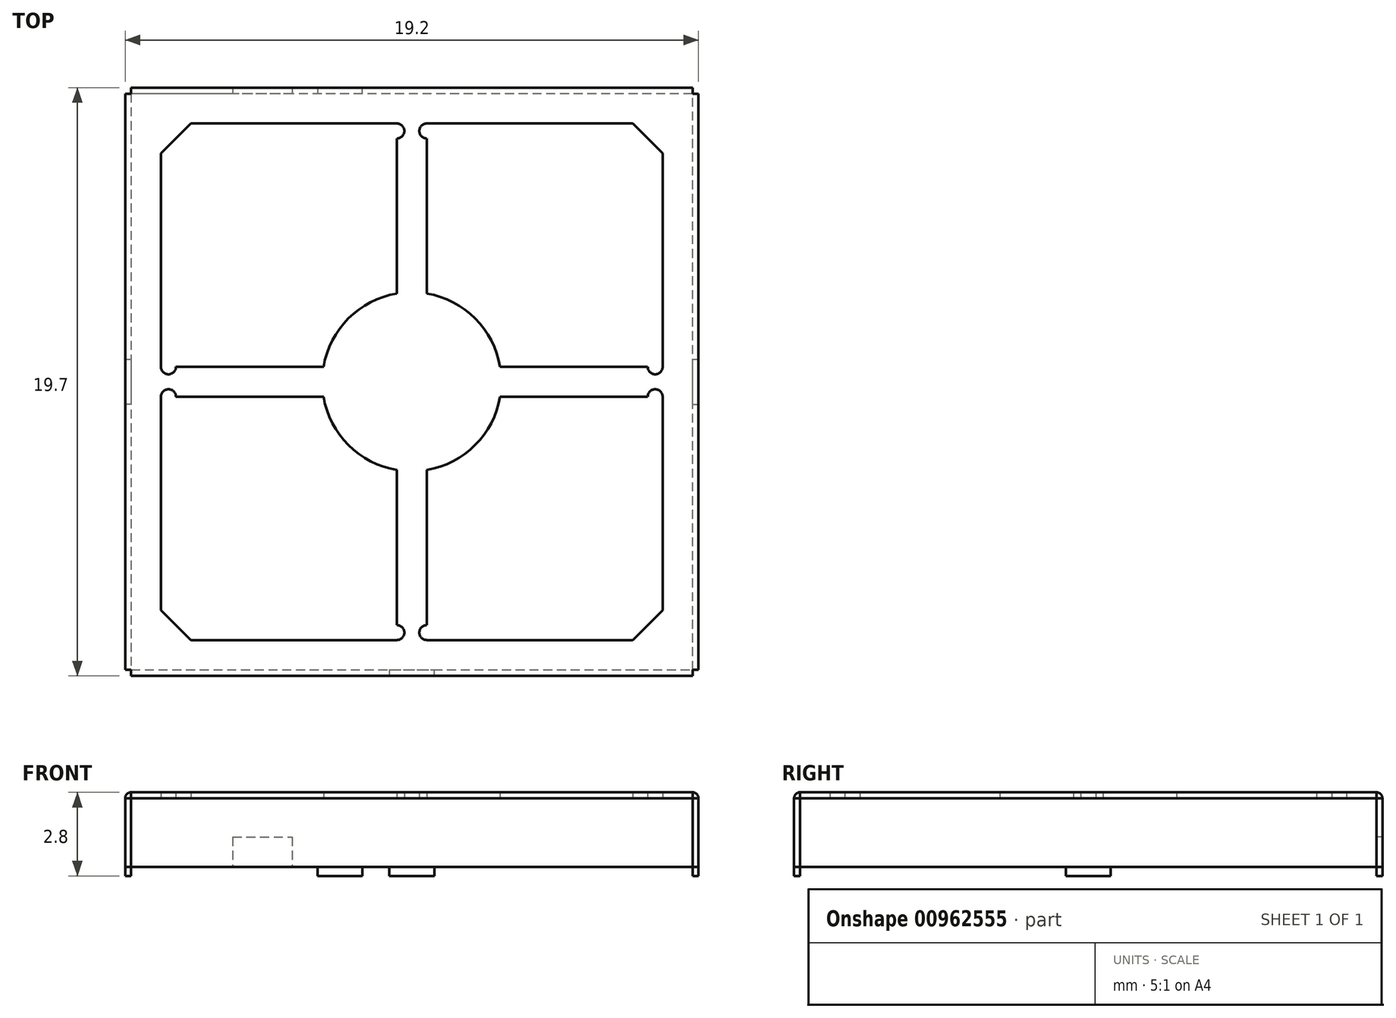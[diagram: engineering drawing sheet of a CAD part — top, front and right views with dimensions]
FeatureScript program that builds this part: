
annotation { "Feature Type Name" : "Feature", "Feature Type Description" : "" }
export const myFeature = defineFeature(function(context is Context, id is Id, definition is map)
    precondition{}
    {
        {
            var Q0;
            Q0=qCreatedBy(makeId("Top.planeOp"),FACE);
            var sketch = newSketch(context, id + "F0", { "sketchPlane" : qUnion([Q0])});
            skLineSegment(sketch, "E0", {"start": v(-9.4, 9.85) * mm, "end": v(9.4, 9.85) * mm});
            skLineSegment(sketch, "E1", {"start": v(-9.6, 9.65) * mm, "end": v(-9.4, 9.65) * mm});
            skLineSegment(sketch, "E2", {"start": v(-9.4, 9.65) * mm, "end": v(-9.4, 9.85) * mm});
            skLineSegment(sketch, "E3", {"start": v(9.6, 9.65) * mm, "end": v(9.4, 9.65) * mm});
            skLineSegment(sketch, "E4", {"start": v(9.4, 9.65) * mm, "end": v(9.4, 9.85) * mm});
            skLineSegment(sketch, "E5", {"start": v(9.6, -9.65) * mm, "end": v(9.4, -9.65) * mm});
            skLineSegment(sketch, "E6", {"start": v(9.4, -9.65) * mm, "end": v(9.4, -9.85) * mm});
            skLineSegment(sketch, "E7", {"start": v(-9.6, -9.65) * mm, "end": v(-9.4, -9.65) * mm});
            skLineSegment(sketch, "E8", {"start": v(-9.4, -9.65) * mm, "end": v(-9.4, -9.85) * mm});
            skLineSegment(sketch, "E9", {"start": v(9.6, 9.65) * mm, "end": v(9.6, -9.65) * mm});
            skLineSegment(sketch, "E10", {"start": v(9.4, -9.85) * mm, "end": v(-9.4, -9.85) * mm});
            skLineSegment(sketch, "E11", {"start": v(-9.6, -9.65) * mm, "end": v(-9.6, 9.65) * mm});
            skLineSegment(sketch, "E12", {"start": v(-9.4, 9.65) * mm, "end": v(-9.4, -9.65) * mm});
            skLineSegment(sketch, "E13", {"start": v(-9.4, -9.65) * mm, "end": v(9.4, -9.65) * mm});
            skLineSegment(sketch, "E14", {"start": v(9.4, -9.65) * mm, "end": v(9.4, 9.65) * mm});
            skLineSegment(sketch, "E15", {"start": v(9.4, 9.65) * mm, "end": v(-9.4, 9.65) * mm});
            skLineSegment(sketch, "E16", {"start": v(-3.15, 9.85) * mm, "end": v(-3.15, 9.65) * mm});
            skLineSegment(sketch, "E17", {"start": v(-1.65, 9.65) * mm, "end": v(-1.65, 9.85) * mm});
            skLineSegment(sketch, "E18", {"start": v(-0.75, -9.65) * mm, "end": v(-0.75, -9.85) * mm});
            skLineSegment(sketch, "E19", {"start": v(0.75, -9.85) * mm, "end": v(0.75, -9.65) * mm});
            skLineSegment(sketch, "E20", {"start": v(-9.6, 0.75) * mm, "end": v(-9.4, 0.75) * mm});
            skLineSegment(sketch, "E21", {"start": v(-9.4, -0.75) * mm, "end": v(-9.6, -0.75) * mm});
            skLineSegment(sketch, "E22", {"start": v(9.4, -0.75) * mm, "end": v(9.6, -0.75) * mm});
            skLineSegment(sketch, "E23", {"start": v(9.4, 0.75) * mm, "end": v(9.6, 0.75) * mm});
            skLineSegment(sketch, "E24", {"start": v(-6, 9.85) * mm, "end": v(-6, 9.65) * mm});
            skLineSegment(sketch, "E25", {"start": v(-4, 9.85) * mm, "end": v(-4, 9.65) * mm});
            skLineSegment(sketch, "E26", {"start": v(-8.4, 7.65) * mm, "end": v(-7.4, 8.65) * mm});
            skLineSegment(sketch, "E27", {"start": v(7.4, 8.65) * mm, "end": v(8.4, 7.65) * mm});
            skLineSegment(sketch, "E28", {"start": v(7.4, -8.65) * mm, "end": v(8.4, -7.65) * mm});
            skLineSegment(sketch, "E29", {"start": v(-7.4, -8.65) * mm, "end": v(-8.4, -7.65) * mm});
            skLineSegment(sketch, "E30", {"start": v(0.5, -2.96) * mm, "end": v(0.5, -8.15) * mm});
            skLineSegment(sketch, "E31", {"start": v(-0.5, -2.96) * mm, "end": v(-0.5, -8.15) * mm});
            skLineSegment(sketch, "E32", {"start": v(2.96, -0.5) * mm, "end": v(7.9, -0.5) * mm});
            skLineSegment(sketch, "E33", {"start": v(-2.96, -0.5) * mm, "end": v(-7.9, -0.5) * mm});
            skLineSegment(sketch, "E34", {"start": v(2.96, 0.5) * mm, "end": v(7.9, 0.5) * mm});
            skLineSegment(sketch, "E35", {"start": v(-2.96, 0.5) * mm, "end": v(-7.9, 0.5) * mm});
            skArc(sketch, "E36", {"start": v(-0.5, 2.96) * mm, "mid": v(-2.12, 2.12) * mm, "end": v(-2.96, 0.5) * mm});
            skArc(sketch, "E37", {"start": v(2.96, 0.5) * mm, "mid": v(2.12, 2.12) * mm, "end": v(0.5, 2.96) * mm});
            skArc(sketch, "E38", {"start": v(0.5, -2.96) * mm, "mid": v(2.12, -2.12) * mm, "end": v(2.96, -0.5) * mm});
            skLineSegment(sketch, "E39", {"start": v(-8.4, -0.5) * mm, "end": v(-8.4, -7.65) * mm});
            skArc(sketch, "E40", {"start": v(-2.96, -0.5) * mm, "mid": v(-2.12, -2.12) * mm, "end": v(-0.5, -2.96) * mm});
            skLineSegment(sketch, "E41", {"start": v(-0.5, 8.65) * mm, "end": v(-7.4, 8.65) * mm});
            skLineSegment(sketch, "E42", {"start": v(-8.4, 7.65) * mm, "end": v(-8.4, 0.5) * mm});
            skLineSegment(sketch, "E43", {"start": v(8.4, 0.5) * mm, "end": v(8.4, 7.65) * mm});
            skLineSegment(sketch, "E44", {"start": v(7.4, 8.65) * mm, "end": v(0.5, 8.65) * mm});
            skLineSegment(sketch, "E45", {"start": v(8.4, -7.65) * mm, "end": v(8.4, -0.5) * mm});
            skLineSegment(sketch, "E46", {"start": v(0.5, -8.65) * mm, "end": v(7.4, -8.65) * mm});
            skLineSegment(sketch, "E47", {"start": v(-7.4, -8.65) * mm, "end": v(-0.5, -8.65) * mm});
            skArc(sketch, "E48", {"start": v(0.5, -8.15) * mm, "mid": v(0.25, -8.4) * mm, "end": v(0.5, -8.65) * mm});
            skArc(sketch, "E49", {"start": v(-0.5, -8.65) * mm, "mid": v(-0.25, -8.4) * mm, "end": v(-0.5, -8.15) * mm});
            skLineSegment(sketch, "E50", {"start": v(0.5, 2.96) * mm, "end": v(0.5, 8.15) * mm});
            skLineSegment(sketch, "E51", {"start": v(-0.5, 2.96) * mm, "end": v(-0.5, 8.15) * mm});
            skArc(sketch, "E52", {"start": v(0.5, 8.65) * mm, "mid": v(0.25, 8.4) * mm, "end": v(0.5, 8.15) * mm});
            skArc(sketch, "E53", {"start": v(-0.5, 8.15) * mm, "mid": v(-0.25, 8.4) * mm, "end": v(-0.5, 8.65) * mm});
            skArc(sketch, "E54", {"start": v(7.9, 0.5) * mm, "mid": v(8.15, 0.25) * mm, "end": v(8.4, 0.5) * mm});
            skArc(sketch, "E55", {"start": v(8.4, -0.5) * mm, "mid": v(8.15, -0.25) * mm, "end": v(7.9, -0.5) * mm});
            skArc(sketch, "E56", {"start": v(-8.4, 0.5) * mm, "mid": v(-8.15, 0.25) * mm, "end": v(-7.9, 0.5) * mm});
            skArc(sketch, "E57", {"start": v(-7.9, -0.5) * mm, "mid": v(-8.15, -0.25) * mm, "end": v(-8.4, -0.5) * mm});
            skSolve(sketch);
        }
        {
            var Q0;
            Q0=makeQuery(id+"F0.imprint","IMPRINT",FACE,{"disambiguationData":[TD([[makeQuery(id+"F0.imprint","IMPRINT",EDGE,{"derivedFrom":sQuery(id+"F0.wireOp",EDGE,"E26")}),1.0]])]});
            var Q1;
            {var subQ0=sQuery(id+"F0.wireOp",EDGE,"E8");Q1=makeQuery(id+"F0.imprint","IMPRINT",FACE,{"disambiguationData":[TD([[makeQuery(id+"F0.imprint","IMPRINT",EDGE,{"derivedFrom":subQ0}),1.0]])]});}
            var Q2;
            {var subQ0=sQuery(id+"F0.wireOp",EDGE,"E18");Q2=makeQuery(id+"F0.imprint","IMPRINT",FACE,{"disambiguationData":[TD([[makeQuery(id+"F0.imprint","IMPRINT",EDGE,{"derivedFrom":subQ0}),1.0]])]});}
            var Q3;
            {var subQ0=sQuery(id+"F0.wireOp",EDGE,"E6");Q3=makeQuery(id+"F0.imprint","IMPRINT",FACE,{"disambiguationData":[TD([[makeQuery(id+"F0.imprint","IMPRINT",EDGE,{"derivedFrom":subQ0}),-1.0]])]});}
            var Q4;
            {var subQ0=sQuery(id+"F0.wireOp",EDGE,"E5");Q4=makeQuery(id+"F0.imprint","IMPRINT",FACE,{"disambiguationData":[TD([[makeQuery(id+"F0.imprint","IMPRINT",EDGE,{"derivedFrom":subQ0}),-1.0]])]});}
            var Q5;
            {var subQ0=sQuery(id+"F0.wireOp",EDGE,"E22");Q5=makeQuery(id+"F0.imprint","IMPRINT",FACE,{"disambiguationData":[TD([[makeQuery(id+"F0.imprint","IMPRINT",EDGE,{"derivedFrom":subQ0}),1.0]])]});}
            var Q6;
            {var subQ0=sQuery(id+"F0.wireOp",EDGE,"E3");Q6=makeQuery(id+"F0.imprint","IMPRINT",FACE,{"disambiguationData":[TD([[makeQuery(id+"F0.imprint","IMPRINT",EDGE,{"derivedFrom":subQ0}),1.0]])]});}
            var Q7;
            {var subQ0=sQuery(id+"F0.wireOp",EDGE,"E4");Q7=makeQuery(id+"F0.imprint","IMPRINT",FACE,{"disambiguationData":[TD([[makeQuery(id+"F0.imprint","IMPRINT",EDGE,{"derivedFrom":subQ0}),1.0]])]});}
            var Q8;
            {var subQ0=sQuery(id+"F0.wireOp",EDGE,"E16");Q8=makeQuery(id+"F0.imprint","IMPRINT",FACE,{"disambiguationData":[TD([[makeQuery(id+"F0.imprint","IMPRINT",EDGE,{"derivedFrom":subQ0}),1.0]])]});}
            var Q9;
            {var subQ0=sQuery(id+"F0.wireOp",EDGE,"E16");Q9=makeQuery(id+"F0.imprint","IMPRINT",FACE,{"disambiguationData":[TD([[makeQuery(id+"F0.imprint","IMPRINT",EDGE,{"derivedFrom":subQ0}),-1.0]])]});}
            var Q10;
            {var subQ0=sQuery(id+"F0.wireOp",EDGE,"E24");Q10=makeQuery(id+"F0.imprint","IMPRINT",FACE,{"disambiguationData":[TD([[makeQuery(id+"F0.imprint","IMPRINT",EDGE,{"derivedFrom":subQ0}),1.0]])]});}
            var Q11;
            {var subQ0=sQuery(id+"F0.wireOp",EDGE,"E2");Q11=makeQuery(id+"F0.imprint","IMPRINT",FACE,{"disambiguationData":[TD([[makeQuery(id+"F0.imprint","IMPRINT",EDGE,{"derivedFrom":subQ0}),-1.0]])]});}
            var Q12;
            {var subQ0=sQuery(id+"F0.wireOp",EDGE,"E1");Q12=makeQuery(id+"F0.imprint","IMPRINT",FACE,{"disambiguationData":[TD([[makeQuery(id+"F0.imprint","IMPRINT",EDGE,{"derivedFrom":subQ0}),-1.0]])]});}
            var Q13;
            {var subQ0=sQuery(id+"F0.wireOp",EDGE,"E20");Q13=makeQuery(id+"F0.imprint","IMPRINT",FACE,{"disambiguationData":[TD([[makeQuery(id+"F0.imprint","IMPRINT",EDGE,{"derivedFrom":subQ0}),-1.0]])]});}
            var Q14;
            {var subQ0=sQuery(id+"F0.wireOp",EDGE,"E7");Q14=makeQuery(id+"F0.imprint","IMPRINT",FACE,{"disambiguationData":[TD([[makeQuery(id+"F0.imprint","IMPRINT",EDGE,{"derivedFrom":subQ0}),1.0]])]});}
            extrude(context, id + "F1", {"entities" : qUnion([Q0, Q1, Q2, Q3, Q4, Q5, Q6, Q7, Q8, Q9, Q10, Q11, Q12, Q13, Q14]), "depth" : 2.5 * mm, "offsetDistance" : 25 * mm, "hasSecondDirection" : true, "secondDirectionOppositeDirection" : false, "secondDirectionDepth" : 2.3 * mm});
        }
        {
            var Q0;
            {var subQ0=sQuery(id+"F0.wireOp",EDGE,"E8");Q0=makeQuery(id+"F0.imprint","IMPRINT",FACE,{"disambiguationData":[TD([[makeQuery(id+"F0.imprint","IMPRINT",EDGE,{"derivedFrom":subQ0}),1.0]])]});}
            var Q1;
            {var subQ0=sQuery(id+"F0.wireOp",EDGE,"E18");Q1=makeQuery(id+"F0.imprint","IMPRINT",FACE,{"disambiguationData":[TD([[makeQuery(id+"F0.imprint","IMPRINT",EDGE,{"derivedFrom":subQ0}),1.0]])]});}
            var Q2;
            {var subQ0=sQuery(id+"F0.wireOp",EDGE,"E6");Q2=makeQuery(id+"F0.imprint","IMPRINT",FACE,{"disambiguationData":[TD([[makeQuery(id+"F0.imprint","IMPRINT",EDGE,{"derivedFrom":subQ0}),-1.0]])]});}
            var Q3;
            {var subQ0=sQuery(id+"F0.wireOp",EDGE,"E5");Q3=makeQuery(id+"F0.imprint","IMPRINT",FACE,{"disambiguationData":[TD([[makeQuery(id+"F0.imprint","IMPRINT",EDGE,{"derivedFrom":subQ0}),-1.0]])]});}
            var Q4;
            {var subQ0=sQuery(id+"F0.wireOp",EDGE,"E22");Q4=makeQuery(id+"F0.imprint","IMPRINT",FACE,{"disambiguationData":[TD([[makeQuery(id+"F0.imprint","IMPRINT",EDGE,{"derivedFrom":subQ0}),1.0]])]});}
            var Q5;
            {var subQ0=sQuery(id+"F0.wireOp",EDGE,"E3");Q5=makeQuery(id+"F0.imprint","IMPRINT",FACE,{"disambiguationData":[TD([[makeQuery(id+"F0.imprint","IMPRINT",EDGE,{"derivedFrom":subQ0}),1.0]])]});}
            var Q6;
            {var subQ0=sQuery(id+"F0.wireOp",EDGE,"E4");Q6=makeQuery(id+"F0.imprint","IMPRINT",FACE,{"disambiguationData":[TD([[makeQuery(id+"F0.imprint","IMPRINT",EDGE,{"derivedFrom":subQ0}),1.0]])]});}
            var Q7;
            {var subQ0=sQuery(id+"F0.wireOp",EDGE,"E16");Q7=makeQuery(id+"F0.imprint","IMPRINT",FACE,{"disambiguationData":[TD([[makeQuery(id+"F0.imprint","IMPRINT",EDGE,{"derivedFrom":subQ0}),1.0]])]});}
            var Q8;
            {var subQ0=sQuery(id+"F0.wireOp",EDGE,"E16");Q8=makeQuery(id+"F0.imprint","IMPRINT",FACE,{"disambiguationData":[TD([[makeQuery(id+"F0.imprint","IMPRINT",EDGE,{"derivedFrom":subQ0}),-1.0]])]});}
            var Q9;
            {var subQ0=sQuery(id+"F0.wireOp",EDGE,"E24");Q9=makeQuery(id+"F0.imprint","IMPRINT",FACE,{"disambiguationData":[TD([[makeQuery(id+"F0.imprint","IMPRINT",EDGE,{"derivedFrom":subQ0}),1.0]])]});}
            var Q10;
            {var subQ0=sQuery(id+"F0.wireOp",EDGE,"E2");Q10=makeQuery(id+"F0.imprint","IMPRINT",FACE,{"disambiguationData":[TD([[makeQuery(id+"F0.imprint","IMPRINT",EDGE,{"derivedFrom":subQ0}),-1.0]])]});}
            var Q11;
            {var subQ0=sQuery(id+"F0.wireOp",EDGE,"E1");Q11=makeQuery(id+"F0.imprint","IMPRINT",FACE,{"disambiguationData":[TD([[makeQuery(id+"F0.imprint","IMPRINT",EDGE,{"derivedFrom":subQ0}),-1.0]])]});}
            var Q12;
            {var subQ0=sQuery(id+"F0.wireOp",EDGE,"E20");Q12=makeQuery(id+"F0.imprint","IMPRINT",FACE,{"disambiguationData":[TD([[makeQuery(id+"F0.imprint","IMPRINT",EDGE,{"derivedFrom":subQ0}),-1.0]])]});}
            var Q13;
            {var subQ0=sQuery(id+"F0.wireOp",EDGE,"E7");Q13=makeQuery(id+"F0.imprint","IMPRINT",FACE,{"disambiguationData":[TD([[makeQuery(id+"F0.imprint","IMPRINT",EDGE,{"derivedFrom":subQ0}),1.0]])]});}
            extrude(context, id + "F2", {"entities" : qUnion([Q0, Q1, Q2, Q3, Q4, Q5, Q6, Q7, Q8, Q9, Q10, Q11, Q12, Q13]), "depth" : 2.3 * mm, "offsetDistance" : 25 * mm});
        }
        {
            var Q0;
            {var subQ0=sQuery(id+"F0.wireOp",EDGE,"E22");Q0=makeQuery(id+"F0.imprint","IMPRINT",FACE,{"disambiguationData":[TD([[makeQuery(id+"F0.imprint","IMPRINT",EDGE,{"derivedFrom":subQ0}),1.0]])]});}
            var Q1;
            {var subQ0=sQuery(id+"F0.wireOp",EDGE,"E18");Q1=makeQuery(id+"F0.imprint","IMPRINT",FACE,{"disambiguationData":[TD([[makeQuery(id+"F0.imprint","IMPRINT",EDGE,{"derivedFrom":subQ0}),1.0]])]});}
            var Q2;
            {var subQ0=sQuery(id+"F0.wireOp",EDGE,"E20");Q2=makeQuery(id+"F0.imprint","IMPRINT",FACE,{"disambiguationData":[TD([[makeQuery(id+"F0.imprint","IMPRINT",EDGE,{"derivedFrom":subQ0}),-1.0]])]});}
            var Q3;
            {var subQ0=sQuery(id+"F0.wireOp",EDGE,"E16");Q3=makeQuery(id+"F0.imprint","IMPRINT",FACE,{"disambiguationData":[TD([[makeQuery(id+"F0.imprint","IMPRINT",EDGE,{"derivedFrom":subQ0}),1.0]])]});}
            extrude(context, id + "F3", {"entities" : qUnion([Q0, Q1, Q2, Q3]), "oppositeDirection" : true, "depth" : 0.3 * mm, "offsetDistance" : 25 * mm});
        }
        {
            var Q0;
            {var subQ0=sQuery(id+"F0.wireOp",EDGE,"E24");Q0=makeQuery(id+"F0.imprint","IMPRINT",FACE,{"disambiguationData":[TD([[makeQuery(id+"F0.imprint","IMPRINT",EDGE,{"derivedFrom":subQ0}),1.0]])]});}
            extrude(context, id + "F4", {"entities" : qUnion([Q0]), "operationType" : NewBodyOperationType.REMOVE, "depth" : 1 * mm, "offsetDistance" : 25 * mm});
        }
        {
            var Q0;
            Q0=makeQuery(id+"F1.opExtrude","CAP_EDGE",EDGE,{"disambiguationData":[OSD([sQuery(id+"F0.wireOp",EDGE,"E10")])],"isStart":false});
            var Q1;
            Q1=makeQuery(id+"F1.opExtrude","CAP_EDGE",EDGE,{"disambiguationData":[OSD([sQuery(id+"F0.wireOp",EDGE,"E9")])],"isStart":false});
            var Q2;
            Q2=makeQuery(id+"F1.opExtrude","CAP_EDGE",EDGE,{"disambiguationData":[OSD([sQuery(id+"F0.wireOp",EDGE,"E0")])],"isStart":false});
            var Q3;
            Q3=makeQuery(id+"F1.opExtrude","CAP_EDGE",EDGE,{"disambiguationData":[OSD([sQuery(id+"F0.wireOp",EDGE,"E11")])],"isStart":false});
            fillet(context, id + "F5", {"entities" : qUnion([Q0, Q1, Q2, Q3]), "tangentPropagation" : true, "radius" : 0.2 * mm, "defaultsChanged" : true, "vertexSettings" : [], "allowEdgeOverflow" : false});
        }
    });
